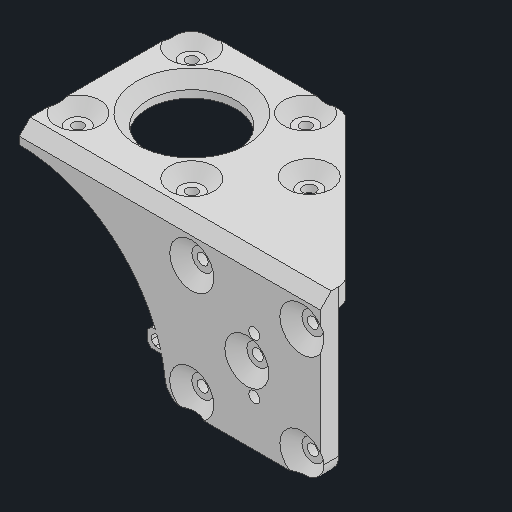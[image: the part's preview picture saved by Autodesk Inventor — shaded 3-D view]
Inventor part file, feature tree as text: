
AUTODESK INVENTOR PART (.ipt)
format: ipt  version: 2025.1 (Build 291241000, 241)  size: 236,032 bytes
history: native  units: mm
features: other x3, sketch x2
ambient origin geometry x8: Origin, YZ Plane, XZ Plane, XY Plane, X Axis, Y Axis, Z Axis, Center Point
bodies: Solid1 (feature_tree)
feature tree (5):
  other  "Tensioner End Bracket.ipt"
  other  "Solid1::Tensioner End Bracket.ipt"
  other  "TaggingFeature1"
  sketch  "Sketch1"  dims[d0=10.0mm]
  sketch  "Sketch2"
